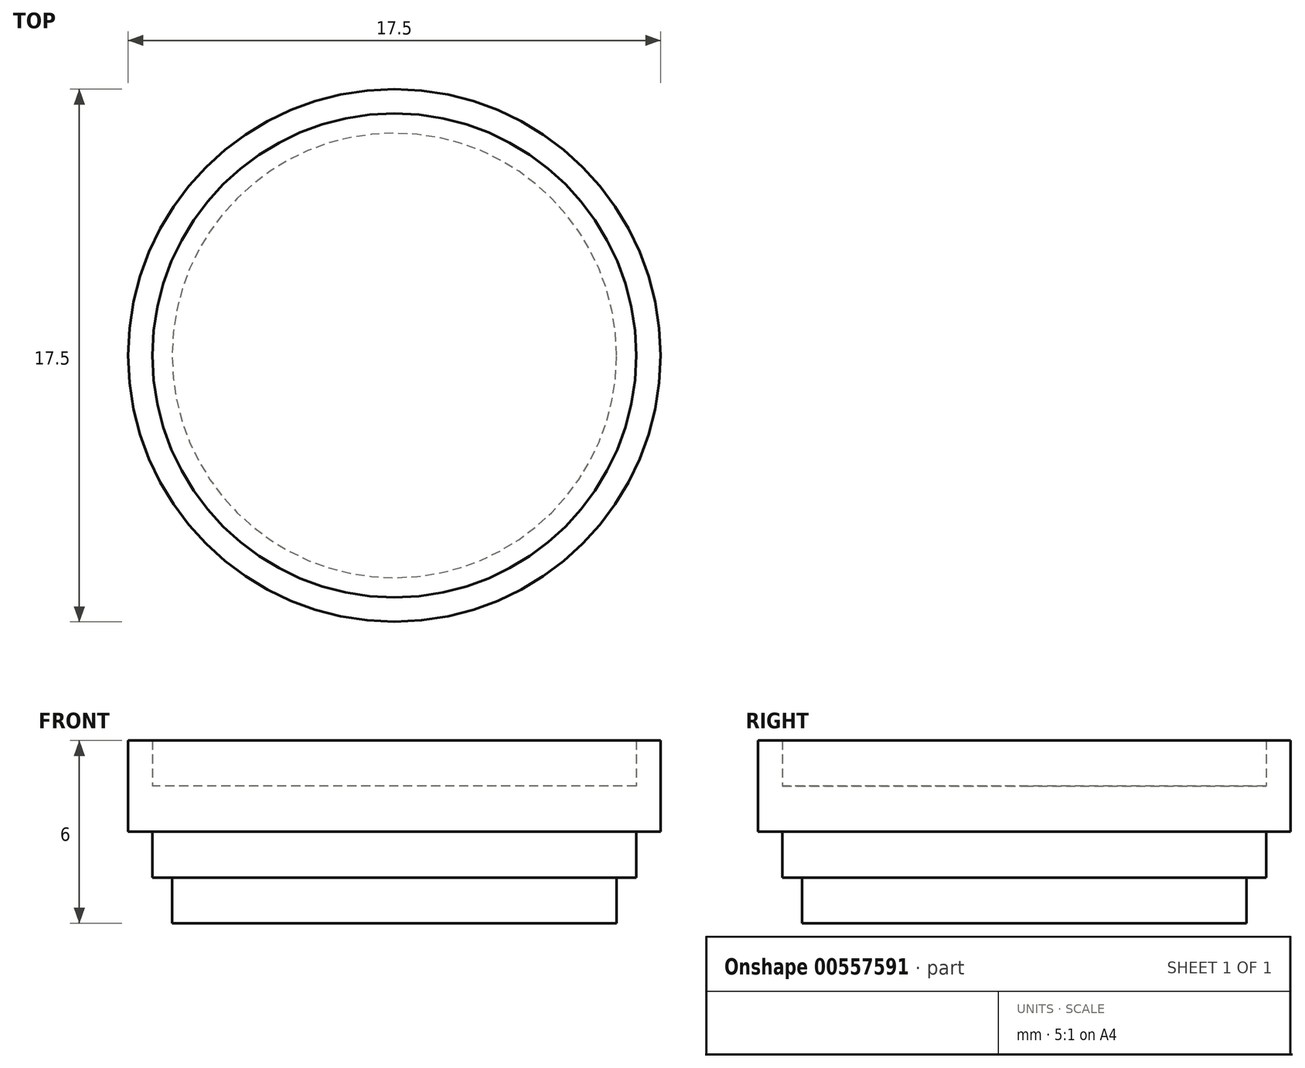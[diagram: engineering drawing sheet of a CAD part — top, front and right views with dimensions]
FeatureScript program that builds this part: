
annotation { "Feature Type Name" : "Feature", "Feature Type Description" : "" }
export const myFeature = defineFeature(function(context is Context, id is Id, definition is map)
    precondition{}
    {
        {
            var Q0;
            Q0=qCreatedBy(makeId("Top.planeOp"),FACE);
            var sketch = newSketch(context, id + "F0", { "sketchPlane" : qUnion([Q0])});
            skCircle(sketch, "E0", {"center": v(0, 0) * mm, "radius": 7.95 * mm});
            skSolve(sketch);
        }
        {
            var Q0;
            Q0=qCreatedBy(makeId("Top.planeOp"),FACE);
            var sketch = newSketch(context, id + "F1", { "sketchPlane" : qUnion([Q0])});
            skSolve(sketch);
        }
        {
            var Q0;
            Q0 = qSketchRegion(id + "F1", true);
            var Q1;
            Q1=makeQuery(id+"F0.imprint","IMPRINT",FACE,{"disambiguationData":[TD([[makeQuery(id+"F0.imprint","IMPRINT",EDGE,{"derivedFrom":sQuery(id+"F0.wireOp",EDGE,"E0")}),1.0]])]});
            extrude(context, id + "F2", {"entities" : qUnion([Q0, Q1]), "depth" : 3 * mm, "offsetDistance" : 25.4 * mm});
        }
        {
            var Q0;
            Q0=qCreatedBy(makeId("Top.planeOp"),FACE);
            var sketch = newSketch(context, id + "F3", { "sketchPlane" : qUnion([Q0])});
            skCircle(sketch, "E1", {"center": v(0, 0) * mm, "radius": 7.3 * mm});
            skSolve(sketch);
        }
        {
            var Q0;
            Q0=makeQuery(id+"F2.opExtrude","CAP_FACE",FACE,{"disambiguationData":[OSD([sQuery(id+"F0.wireOp",EDGE,"E0")])],"isStart":false});
            var sketch = newSketch(context, id + "F4", { "sketchPlane" : qUnion([Q0])});
            skCircle(sketch, "E2", {"center": v(0, 0) * mm, "radius": 8.75 * mm});
            skSolve(sketch);
        }
        {
            var Q0;
            Q0=makeQuery(id+"F4.imprint","IMPRINT",FACE,{"disambiguationData":[TD([[makeQuery(id+"F4.imprint","IMPRINT",EDGE,{"derivedFrom":sQuery(id+"F4.wireOp",EDGE,"E2")}),1.0]])]});
            extrude(context, id + "F5", {"entities" : qUnion([Q0]), "operationType" : NewBodyOperationType.ADD, "endBound" : BoundingType.SYMMETRIC, "depth" : 3 * mm, "offsetDistance" : 25.4 * mm});
        }
        {
            var Q0;
            Q0=makeQuery(id+"F3.imprint","IMPRINT",FACE,{"disambiguationData":[TD([[makeQuery(id+"F3.imprint","IMPRINT",EDGE,{"derivedFrom":sQuery(id+"F3.wireOp",EDGE,"E1")}),1.0]])]});
            extrude(context, id + "F6", {"entities" : qUnion([Q0]), "operationType" : NewBodyOperationType.ADD, "endBound" : BoundingType.SYMMETRIC, "depth" : 3 * mm, "offsetDistance" : 25.4 * mm});
        }
    });
